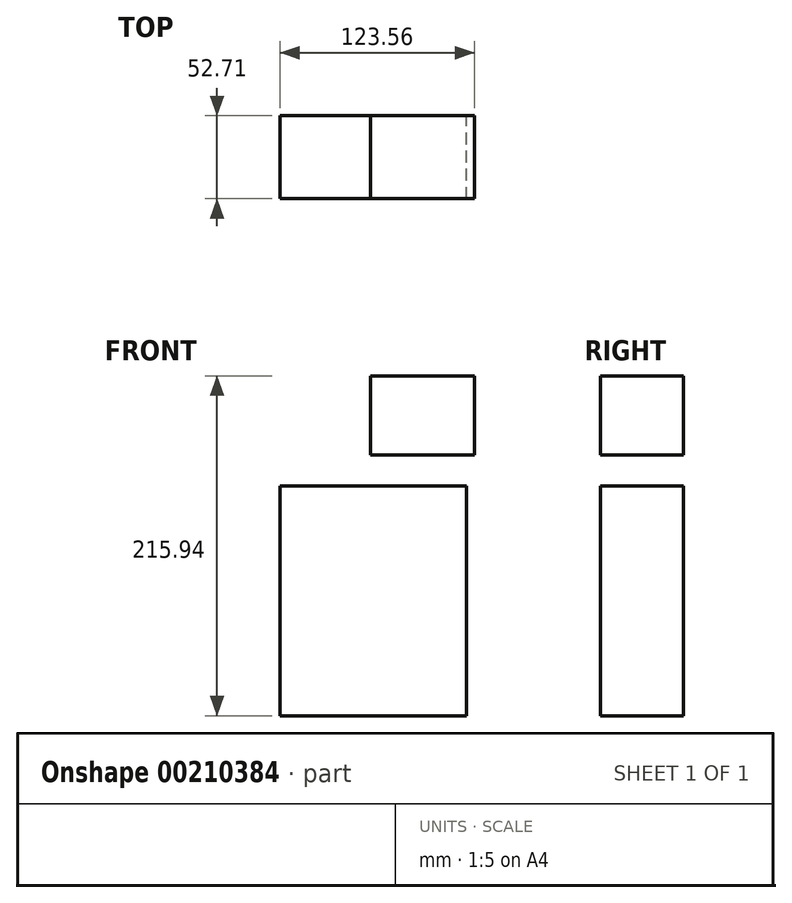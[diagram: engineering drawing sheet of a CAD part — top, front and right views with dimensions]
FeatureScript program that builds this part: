
annotation { "Feature Type Name" : "Feature", "Feature Type Description" : "" }
export const myFeature = defineFeature(function(context is Context, id is Id, definition is map)
    precondition{}
    {
        {
            var Q0;
            Q0=qCreatedBy(makeId("Front.planeOp"),FACE);
            var sketch = newSketch(context, id + "F0", { "sketchPlane" : qUnion([Q0])});
            skLineSegment(sketch, "E0.bottom", {"start": v(16.46, 146.64) * mm, "end": v(82.51, 146.64) * mm});
            skLineSegment(sketch, "E0.top", {"start": v(16.46, 96.33) * mm, "end": v(82.51, 96.33) * mm});
            skLineSegment(sketch, "E0.left", {"start": v(16.46, 146.64) * mm, "end": v(16.46, 96.33) * mm});
            skLineSegment(sketch, "E0.right", {"start": v(82.51, 146.64) * mm, "end": v(82.51, 96.33) * mm});
            skLineSegment(sketch, "E1.bottom", {"start": v(-41.05, 76.7) * mm, "end": v(77.5, 76.7) * mm});
            skLineSegment(sketch, "E1.top", {"start": v(-41.05, -69.3) * mm, "end": v(77.5, -69.3) * mm});
            skLineSegment(sketch, "E1.left", {"start": v(-41.05, 76.7) * mm, "end": v(-41.05, -69.3) * mm});
            skLineSegment(sketch, "E1.right", {"start": v(77.5, 76.7) * mm, "end": v(77.5, -69.3) * mm});
            skSolve(sketch);
        }
        {
            var Q0;
            Q0 = qSketchRegion(id + "F0", true);
            extrude(context, id + "F1", {"entities" : qUnion([Q0]), "depth" : 52.7 * mm});
        }
    });
